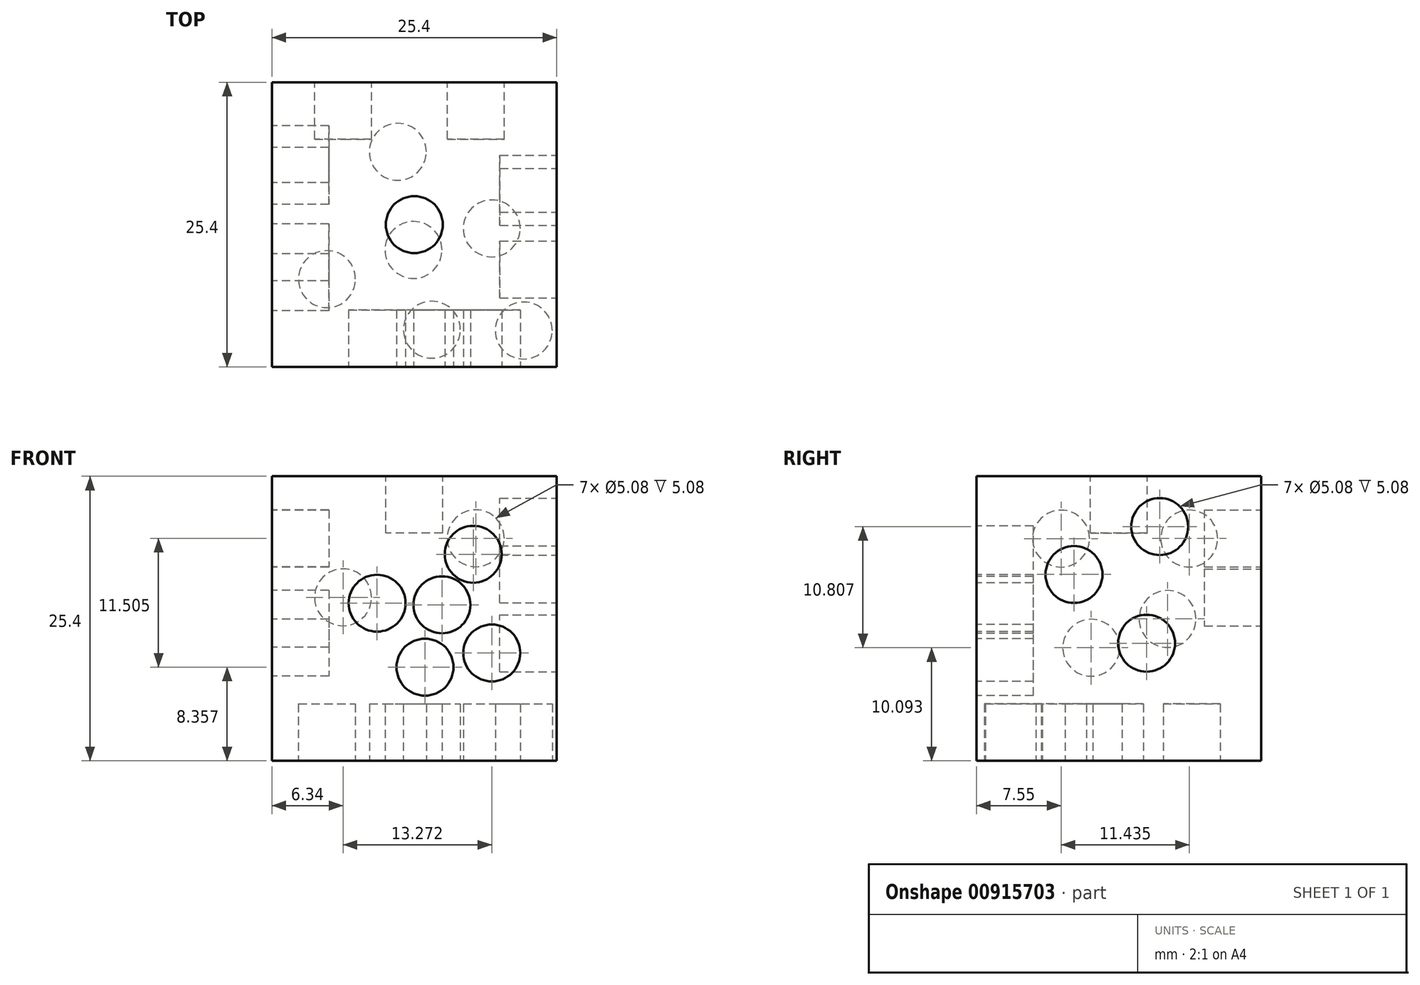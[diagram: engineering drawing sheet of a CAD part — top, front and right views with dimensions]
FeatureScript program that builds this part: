
annotation { "Feature Type Name" : "Feature", "Feature Type Description" : "" }
export const myFeature = defineFeature(function(context is Context, id is Id, definition is map)
    precondition{}
    {
        {
            var Q0;
            Q0=qCreatedBy(makeId("Top.planeOp"),FACE);
            var sketch = newSketch(context, id + "F0", { "sketchPlane" : qUnion([Q0])});
            skLineSegment(sketch, "E0.bottom", {"start": v(-72.3, 69.58) * mm, "end": v(-46.9, 69.58) * mm});
            skLineSegment(sketch, "E0.top", {"start": v(-72.3, 44.18) * mm, "end": v(-46.9, 44.18) * mm});
            skLineSegment(sketch, "E0.left", {"start": v(-72.3, 69.58) * mm, "end": v(-72.3, 44.18) * mm});
            skLineSegment(sketch, "E0.right", {"start": v(-46.9, 69.58) * mm, "end": v(-46.9, 44.18) * mm});
            skSolve(sketch);
        }
        {
            var Q0;
            Q0 = qSketchRegion(id + "F0", true);
            extrude(context, id + "F1", {"entities" : qUnion([Q0]), "depth" : 25.4 * mm, "offsetDistance" : 25.4 * mm});
        }
        {
            var Q0;
            Q0=makeQuery(id+"F1.opExtrude","CAP_FACE",FACE,{"disambiguationData":[OSD([sQuery(id+"F0.wireOp",EDGE,"E0.bottom"),sQuery(id+"F0.wireOp",EDGE,"E0.top"),sQuery(id+"F0.wireOp",EDGE,"E0.left"),sQuery(id+"F0.wireOp",EDGE,"E0.right")])],"isStart":false});
            var sketch = newSketch(context, id + "F2", { "sketchPlane" : qUnion([Q0])});
            skCircle(sketch, "E1", {"center": v(-59.6, 56.88) * mm, "radius": 2.54 * mm});
            skSolve(sketch);
        }
        {
            var Q0;
            Q0=makeQuery(id+"F2.imprint","IMPRINT",FACE,{"disambiguationData":[TD([[makeQuery(id+"F2.imprint","IMPRINT",EDGE,{"derivedFrom":sQuery(id+"F2.wireOp",EDGE,"E1")}),1.0]])]});
            extrude(context, id + "F3", {"entities" : qUnion([Q0]), "operationType" : NewBodyOperationType.REMOVE, "oppositeDirection" : true, "depth" : 5.08 * mm, "offsetDistance" : 25.4 * mm});
        }
        {
            var Q0;
            Q0=makeQuery(id+"F1.opExtrude","CAP_FACE",FACE,{"disambiguationData":[OSD([sQuery(id+"F0.wireOp",EDGE,"E0.bottom"),sQuery(id+"F0.wireOp",EDGE,"E0.top"),sQuery(id+"F0.wireOp",EDGE,"E0.left"),sQuery(id+"F0.wireOp",EDGE,"E0.right")])],"isStart":true});
            var sketch = newSketch(context, id + "F4", { "sketchPlane" : qUnion([Q0])});
            skCircle(sketch, "E2", {"center": v(-49.84, -47.43) * mm, "radius": 2.54 * mm});
            skCircle(sketch, "E3", {"center": v(-52.7, -56.55) * mm, "radius": 2.54 * mm});
            skCircle(sketch, "E4", {"center": v(-58.04, -47.5) * mm, "radius": 2.54 * mm});
            skCircle(sketch, "E5", {"center": v(-59.68, -54.62) * mm, "radius": 2.54 * mm});
            skCircle(sketch, "E6", {"center": v(-61.08, -63.38) * mm, "radius": 2.54 * mm});
            skCircle(sketch, "E7", {"center": v(-67.4, -52.02) * mm, "radius": 2.54 * mm});
            skSolve(sketch);
        }
        {
            var Q0;
            Q0=makeQuery(id+"F4.imprint","IMPRINT",FACE,{"disambiguationData":[TD([[makeQuery(id+"F4.imprint","IMPRINT",EDGE,{"derivedFrom":sQuery(id+"F4.wireOp",EDGE,"E2")}),1.0]])]});
            var Q1;
            Q1=makeQuery(id+"F4.imprint","IMPRINT",FACE,{"disambiguationData":[TD([[makeQuery(id+"F4.imprint","IMPRINT",EDGE,{"derivedFrom":sQuery(id+"F4.wireOp",EDGE,"E3")}),1.0]])]});
            var Q2;
            Q2=makeQuery(id+"F4.imprint","IMPRINT",FACE,{"disambiguationData":[TD([[makeQuery(id+"F4.imprint","IMPRINT",EDGE,{"derivedFrom":sQuery(id+"F4.wireOp",EDGE,"E6")}),1.0]])]});
            var Q3;
            Q3=makeQuery(id+"F4.imprint","IMPRINT",FACE,{"disambiguationData":[TD([[makeQuery(id+"F4.imprint","IMPRINT",EDGE,{"derivedFrom":sQuery(id+"F4.wireOp",EDGE,"E5")}),1.0]])]});
            var Q4;
            Q4=makeQuery(id+"F4.imprint","IMPRINT",FACE,{"disambiguationData":[TD([[makeQuery(id+"F4.imprint","IMPRINT",EDGE,{"derivedFrom":sQuery(id+"F4.wireOp",EDGE,"E4")}),1.0]])]});
            var Q5;
            Q5=makeQuery(id+"F4.imprint","IMPRINT",FACE,{"disambiguationData":[TD([[makeQuery(id+"F4.imprint","IMPRINT",EDGE,{"derivedFrom":sQuery(id+"F4.wireOp",EDGE,"E7")}),1.0]])]});
            extrude(context, id + "F5", {"entities" : qUnion([Q0, Q1, Q2, Q3, Q4, Q5]), "operationType" : NewBodyOperationType.REMOVE, "oppositeDirection" : true, "depth" : 5.08 * mm, "offsetDistance" : 25.4 * mm});
        }
        {
            var Q0;
            Q0=makeQuery(id+"F1.opExtrude","SWEPT_FACE",FACE,{"disambiguationData":[OSD([sQuery(id+"F0.wireOp",EDGE,"E0.top")])]});
            var sketch = newSketch(context, id + "F6", { "sketchPlane" : qUnion([Q0])});
            skCircle(sketch, "E8", {"center": v(-54.35, 18.43) * mm, "radius": 2.54 * mm});
            skCircle(sketch, "E9", {"center": v(-57.13, 13.92) * mm, "radius": 2.54 * mm});
            skCircle(sketch, "E10", {"center": v(-52.69, 9.63) * mm, "radius": 2.54 * mm});
            skCircle(sketch, "E11", {"center": v(-58.65, 8.36) * mm, "radius": 2.54 * mm});
            skCircle(sketch, "E12", {"center": v(-62.93, 14.07) * mm, "radius": 2.54 * mm});
            skSolve(sketch);
        }
        {
            var Q0;
            Q0=makeQuery(id+"F6.imprint","IMPRINT",FACE,{"disambiguationData":[TD([[makeQuery(id+"F6.imprint","IMPRINT",EDGE,{"derivedFrom":sQuery(id+"F6.wireOp",EDGE,"E8")}),1.0]])]});
            var Q1;
            Q1=makeQuery(id+"F6.imprint","IMPRINT",FACE,{"disambiguationData":[TD([[makeQuery(id+"F6.imprint","IMPRINT",EDGE,{"derivedFrom":sQuery(id+"F6.wireOp",EDGE,"E9")}),1.0]])]});
            var Q2;
            Q2=makeQuery(id+"F6.imprint","IMPRINT",FACE,{"disambiguationData":[TD([[makeQuery(id+"F6.imprint","IMPRINT",EDGE,{"derivedFrom":sQuery(id+"F6.wireOp",EDGE,"E12")}),1.0]])]});
            var Q3;
            Q3=makeQuery(id+"F6.imprint","IMPRINT",FACE,{"disambiguationData":[TD([[makeQuery(id+"F6.imprint","IMPRINT",EDGE,{"derivedFrom":sQuery(id+"F6.wireOp",EDGE,"E10")}),1.0]])]});
            var Q4;
            Q4=makeQuery(id+"F6.imprint","IMPRINT",FACE,{"disambiguationData":[TD([[makeQuery(id+"F6.imprint","IMPRINT",EDGE,{"derivedFrom":sQuery(id+"F6.wireOp",EDGE,"E11")}),1.0]])]});
            extrude(context, id + "F7", {"entities" : qUnion([Q0, Q1, Q2, Q3, Q4]), "operationType" : NewBodyOperationType.REMOVE, "oppositeDirection" : true, "depth" : 5.08 * mm, "offsetDistance" : 25.4 * mm});
        }
        {
            var Q0;
            Q0=makeQuery(id+"F1.opExtrude","SWEPT_FACE",FACE,{"disambiguationData":[OSD([sQuery(id+"F0.wireOp",EDGE,"E0.bottom")])]});
            var sketch = newSketch(context, id + "F8", { "sketchPlane" : qUnion([Q0])});
            skCircle(sketch, "E13", {"center": v(54.12, 19.86) * mm, "radius": 2.54 * mm});
            skCircle(sketch, "E14", {"center": v(65.96, 14.59) * mm, "radius": 2.54 * mm});
            skSolve(sketch);
        }
        {
            var Q0;
            Q0=makeQuery(id+"F8.imprint","IMPRINT",FACE,{"disambiguationData":[TD([[makeQuery(id+"F8.imprint","IMPRINT",EDGE,{"derivedFrom":sQuery(id+"F8.wireOp",EDGE,"E13")}),1.0]])]});
            var Q1;
            Q1=makeQuery(id+"F8.imprint","IMPRINT",FACE,{"disambiguationData":[TD([[makeQuery(id+"F8.imprint","IMPRINT",EDGE,{"derivedFrom":sQuery(id+"F8.wireOp",EDGE,"E14")}),1.0]])]});
            extrude(context, id + "F9", {"entities" : qUnion([Q0, Q1]), "operationType" : NewBodyOperationType.REMOVE, "oppositeDirection" : true, "depth" : 5.08 * mm, "offsetDistance" : 25.4 * mm});
        }
        {
            var Q0;
            Q0=makeQuery(id+"F1.opExtrude","SWEPT_FACE",FACE,{"disambiguationData":[OSD([sQuery(id+"F0.wireOp",EDGE,"E0.left")])]});
            var sketch = newSketch(context, id + "F10", { "sketchPlane" : qUnion([Q0])});
            skCircle(sketch, "E15", {"center": v(-63.16, 19.84) * mm, "radius": 2.54 * mm});
            skCircle(sketch, "E16", {"center": v(-54.42, 10.1) * mm, "radius": 2.54 * mm});
            skCircle(sketch, "E17", {"center": v(-61.23, 12.66) * mm, "radius": 2.54 * mm});
            skCircle(sketch, "E18", {"center": v(-51.73, 19.83) * mm, "radius": 2.54 * mm});
            skSolve(sketch);
        }
        {
            var Q0;
            Q0=makeQuery(id+"F10.imprint","IMPRINT",FACE,{"disambiguationData":[TD([[makeQuery(id+"F10.imprint","IMPRINT",EDGE,{"derivedFrom":sQuery(id+"F10.wireOp",EDGE,"E17")}),1.0]])]});
            var Q1;
            Q1=makeQuery(id+"F10.imprint","IMPRINT",FACE,{"disambiguationData":[TD([[makeQuery(id+"F10.imprint","IMPRINT",EDGE,{"derivedFrom":sQuery(id+"F10.wireOp",EDGE,"E16")}),1.0]])]});
            var Q2;
            Q2=makeQuery(id+"F10.imprint","IMPRINT",FACE,{"disambiguationData":[TD([[makeQuery(id+"F10.imprint","IMPRINT",EDGE,{"derivedFrom":sQuery(id+"F10.wireOp",EDGE,"E18")}),1.0]])]});
            var Q3;
            Q3=makeQuery(id+"F10.imprint","IMPRINT",FACE,{"disambiguationData":[TD([[makeQuery(id+"F10.imprint","IMPRINT",EDGE,{"derivedFrom":sQuery(id+"F10.wireOp",EDGE,"E15")}),1.0]])]});
            extrude(context, id + "F11", {"entities" : qUnion([Q0, Q1, Q2, Q3]), "operationType" : NewBodyOperationType.REMOVE, "oppositeDirection" : true, "depth" : 5.08 * mm, "offsetDistance" : 25.4 * mm});
        }
        {
            var Q0;
            Q0=makeQuery(id+"F1.opExtrude","SWEPT_FACE",FACE,{"disambiguationData":[OSD([sQuery(id+"F0.wireOp",EDGE,"E0.right")])]});
            var sketch = newSketch(context, id + "F12", { "sketchPlane" : qUnion([Q0])});
            skCircle(sketch, "E19", {"center": v(60.53, 20.9) * mm, "radius": 2.54 * mm});
            skCircle(sketch, "E20", {"center": v(59.36, 10.49) * mm, "radius": 2.54 * mm});
            skCircle(sketch, "E21", {"center": v(52.88, 16.63) * mm, "radius": 2.54 * mm});
            skSolve(sketch);
        }
        {
            var Q0;
            Q0=makeQuery(id+"F12.imprint","IMPRINT",FACE,{"disambiguationData":[TD([[makeQuery(id+"F12.imprint","IMPRINT",EDGE,{"derivedFrom":sQuery(id+"F12.wireOp",EDGE,"E21")}),1.0]])]});
            var Q1;
            Q1=makeQuery(id+"F12.imprint","IMPRINT",FACE,{"disambiguationData":[TD([[makeQuery(id+"F12.imprint","IMPRINT",EDGE,{"derivedFrom":sQuery(id+"F12.wireOp",EDGE,"E20")}),1.0]])]});
            var Q2;
            Q2=makeQuery(id+"F12.imprint","IMPRINT",FACE,{"disambiguationData":[TD([[makeQuery(id+"F12.imprint","IMPRINT",EDGE,{"derivedFrom":sQuery(id+"F12.wireOp",EDGE,"E19")}),1.0]])]});
            extrude(context, id + "F13", {"entities" : qUnion([Q0, Q1, Q2]), "operationType" : NewBodyOperationType.REMOVE, "oppositeDirection" : true, "depth" : 5.08 * mm, "offsetDistance" : 25.4 * mm});
        }
    });
